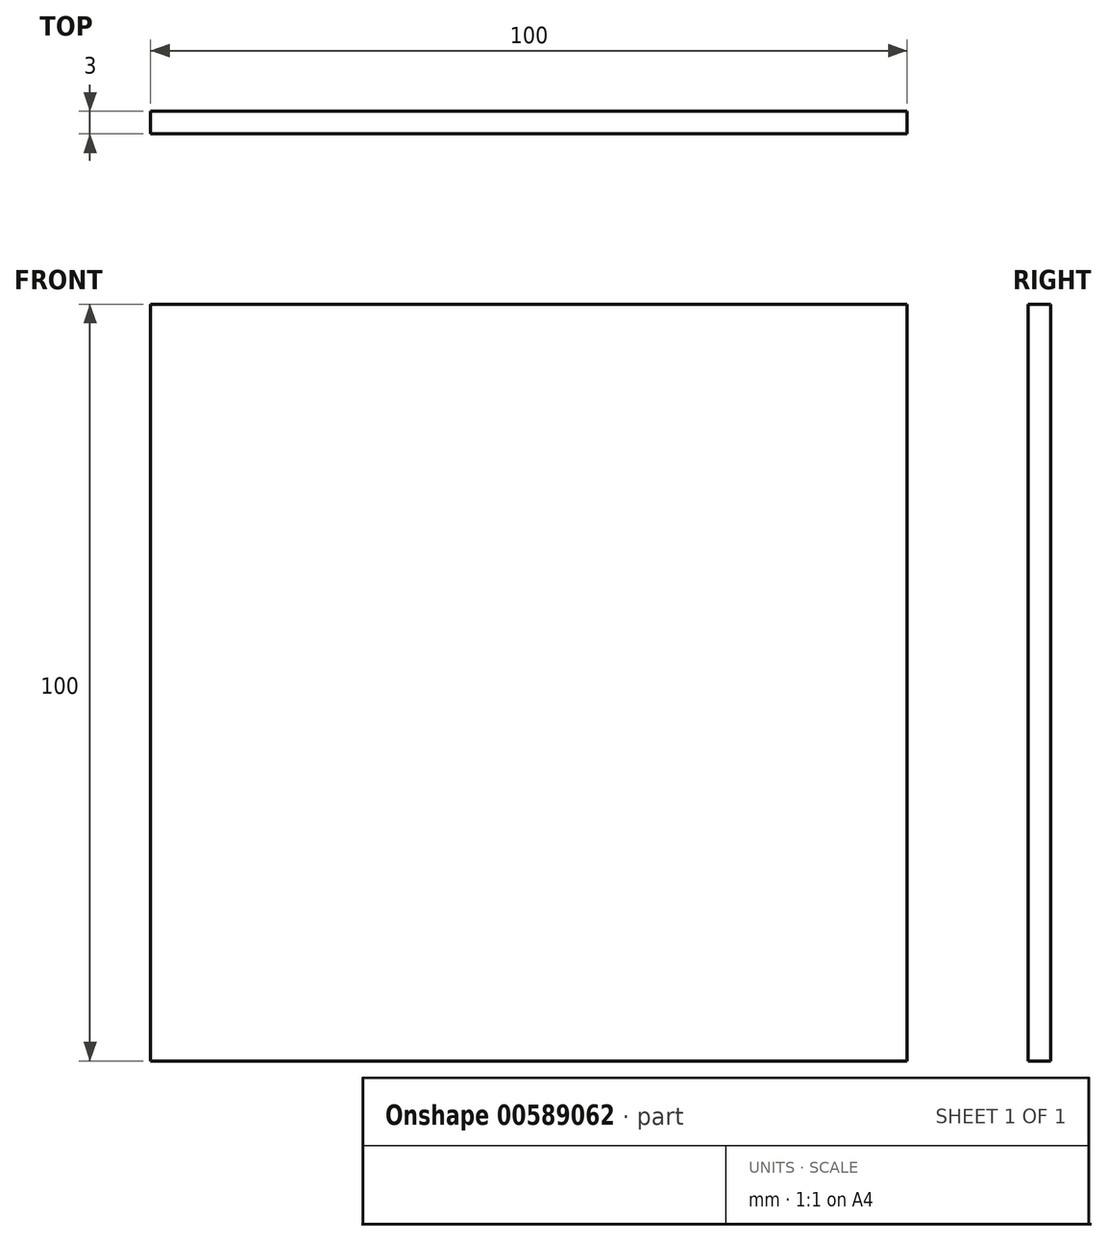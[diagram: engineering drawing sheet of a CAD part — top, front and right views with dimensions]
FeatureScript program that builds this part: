
annotation { "Feature Type Name" : "Feature", "Feature Type Description" : "" }
export const myFeature = defineFeature(function(context is Context, id is Id, definition is map)
    precondition{}
    {
        {
            var Q0;
            Q0=qCreatedBy(makeId("Front.planeOp"),FACE);
            var sketch = newSketch(context, id + "F0", { "sketchPlane" : qUnion([Q0])});
            skLineSegment(sketch, "E0.bottom", {"start": v(-50.91, 74.1) * mm, "end": v(49.09, 74.1) * mm});
            skLineSegment(sketch, "E0.top", {"start": v(-50.91, -25.9) * mm, "end": v(49.09, -25.9) * mm});
            skLineSegment(sketch, "E0.left", {"start": v(-50.91, 74.1) * mm, "end": v(-50.91, -25.9) * mm});
            skLineSegment(sketch, "E0.right", {"start": v(49.09, 74.1) * mm, "end": v(49.09, -25.9) * mm});
            skSolve(sketch);
        }
        {
            var Q0;
            Q0=qSketchRegion(id+"F0",true);
            extrude(context, id + "F1", {"entities" : qUnion([Q0]), "depth" : 3 * mm, "offsetDistance" : 25 * mm});
        }
    });
